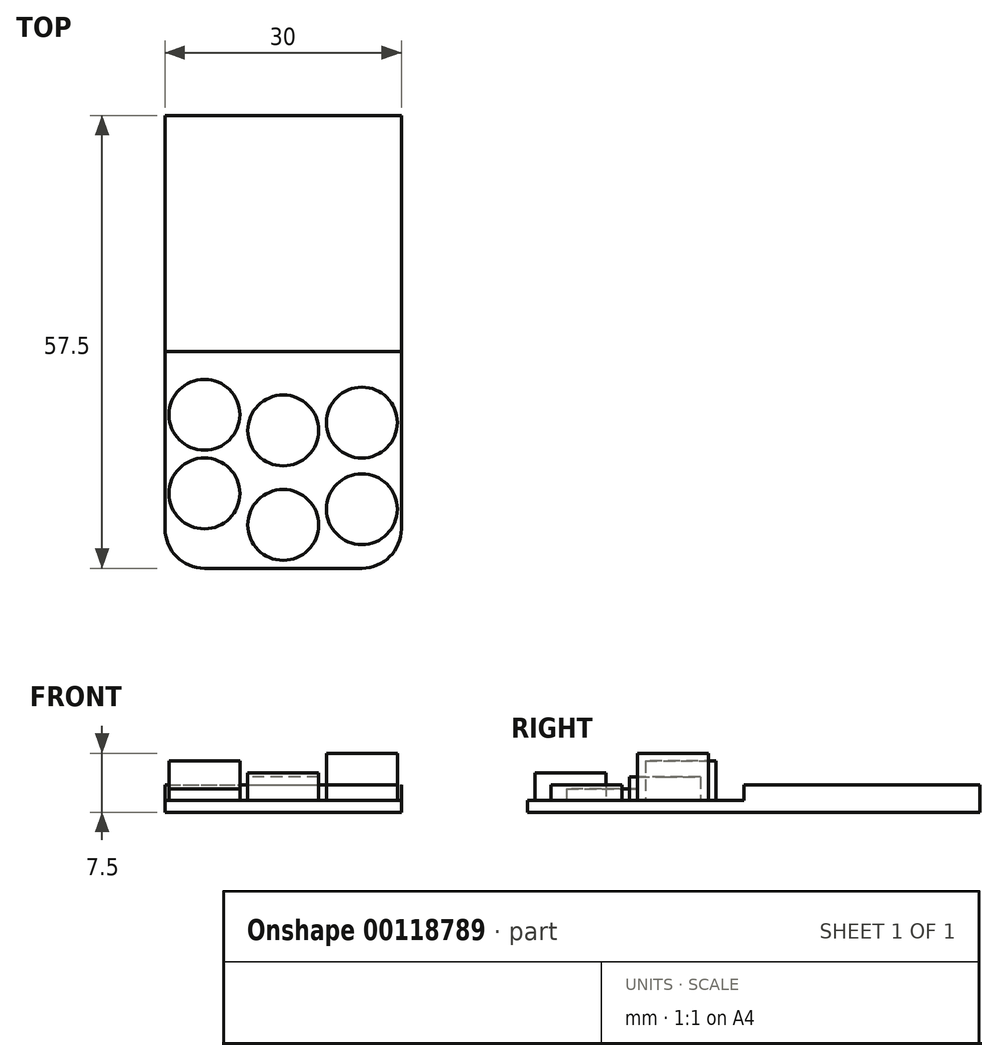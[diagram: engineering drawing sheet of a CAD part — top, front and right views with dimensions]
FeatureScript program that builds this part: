
annotation { "Feature Type Name" : "Feature", "Feature Type Description" : "" }
export const myFeature = defineFeature(function(context is Context, id is Id, definition is map)
    precondition{}
    {
        {
            var Q0;
            Q0=qCreatedBy(makeId("Top.planeOp"),FACE);
            var sketch = newSketch(context, id + "F0", { "sketchPlane" : qUnion([Q0])});
            skLineSegment(sketch, "E0.bottom", {"start": v(-15, 18.18) * mm, "end": v(15, 18.18) * mm});
            skLineSegment(sketch, "E0.top", {"start": v(-15, -11.82) * mm, "end": v(15, -11.82) * mm});
            skLineSegment(sketch, "E0.left", {"start": v(-15, 18.18) * mm, "end": v(-15, -11.82) * mm});
            skLineSegment(sketch, "E0.right", {"start": v(15, 18.18) * mm, "end": v(15, -11.82) * mm});
            skLineSegment(sketch, "E1", {"start": v(0, 18.18) * mm, "end": v(0, -11.82) * mm, "construction": true});
            skLineSegment(sketch, "E2", {"start": v(0, -11.82) * mm, "end": v(0, -39.32) * mm, "construction": true});
            skLineSegment(sketch, "E3", {"start": v(-10, -21.82) * mm, "end": v(10, -21.82) * mm, "construction": true});
            skLineSegment(sketch, "E4", {"start": v(-5, -11.82) * mm, "end": v(-5, -39.32) * mm, "construction": true});
            skLineSegment(sketch, "E5.MirrorCS", {"start": v(5, -11.82) * mm, "end": v(5, -39.32) * mm, "construction": true});
            skLineSegment(sketch, "E6", {"start": v(-10, -11.82) * mm, "end": v(-10, -39.32) * mm, "construction": true});
            skLineSegment(sketch, "E7.MirrorCS", {"start": v(10, -11.82) * mm, "end": v(10, -39.32) * mm, "construction": true});
            skPoint(sketch, "E8.orphan", {"position": v(0, -21.82) * mm});
            skCircle(sketch, "E9", {"center": v(-10, -19.82) * mm, "radius": 4.5 * mm});
            skCircle(sketch, "E10", {"center": v(0, -21.82) * mm, "radius": 4.5 * mm});
            skCircle(sketch, "E11", {"center": v(10, -20.82) * mm, "radius": 4.5 * mm});
            skLineSegment(sketch, "E12", {"start": v(-15, -11.82) * mm, "end": v(-15, -34.32) * mm});
            skLineSegment(sketch, "E13", {"start": v(-10, -39.32) * mm, "end": v(10, -39.32) * mm});
            skLineSegment(sketch, "E14", {"start": v(15, -34.32) * mm, "end": v(15, -11.82) * mm});
            skPoint(sketch, "E15.orphan", {"position": v(-10, -22.85) * mm});
            skPoint(sketch, "E16.orphan", {"position": v(-5, -28.5) * mm});
            skPoint(sketch, "E17.orphan", {"position": v(10, -22.85) * mm});
            skPoint(sketch, "E18.orphan", {"position": v(0, -31.82) * mm});
            skPoint(sketch, "E19.orphan", {"position": v(5, -28.5) * mm});
            skCircle(sketch, "E20", {"center": v(-10, -29.82) * mm, "radius": 4.5 * mm});
            skCircle(sketch, "E21", {"center": v(0, -33.82) * mm, "radius": 4.5 * mm});
            skCircle(sketch, "E22", {"center": v(10, -31.82) * mm, "radius": 4.5 * mm});
            skPoint(sketch, "E23.visualSharp", {"position": v(-15, -39.32) * mm});
            skArc(sketch, "E23.filletArc", {"start": v(-15, -34.32) * mm, "mid": v(-13.54, -37.85) * mm, "end": v(-10, -39.32) * mm});
            skPoint(sketch, "E24.visualSharp", {"position": v(15, -39.32) * mm});
            skArc(sketch, "E24.filletArc", {"start": v(10, -39.32) * mm, "mid": v(13.54, -37.85) * mm, "end": v(15, -34.32) * mm});
            skSolve(sketch);
        }
        {
            var Q0;
            Q0=makeQuery(id+"F0.imprint","IMPRINT",FACE,{"disambiguationData":[TD([[makeQuery(id+"F0.imprint","IMPRINT",EDGE,{"derivedFrom":sQuery(id+"F0.wireOp",EDGE,"E0.bottom")}),-1.0]])]});
            var Q1;
            Q1=makeQuery(id+"F0.imprint","IMPRINT",FACE,{"disambiguationData":[TD([[makeQuery(id+"F0.imprint","IMPRINT",EDGE,{"derivedFrom":sQuery(id+"F0.wireOp",EDGE,"E0.top")}),-1.0]])]});
            var Q2;
            Q2=makeQuery(id+"F0.imprint","IMPRINT",FACE,{"disambiguationData":[TD([[makeQuery(id+"F0.imprint","IMPRINT",EDGE,{"derivedFrom":sQuery(id+"F0.wireOp",EDGE,"E9")}),1.0]])]});
            var Q3;
            Q3=makeQuery(id+"F0.imprint","IMPRINT",FACE,{"disambiguationData":[TD([[makeQuery(id+"F0.imprint","IMPRINT",EDGE,{"derivedFrom":sQuery(id+"F0.wireOp",EDGE,"E10")}),1.0]])]});
            var Q4;
            Q4=makeQuery(id+"F0.imprint","IMPRINT",FACE,{"disambiguationData":[TD([[makeQuery(id+"F0.imprint","IMPRINT",EDGE,{"derivedFrom":sQuery(id+"F0.wireOp",EDGE,"E11")}),1.0]])]});
            var Q5;
            Q5=makeQuery(id+"F0.imprint","IMPRINT",FACE,{"disambiguationData":[TD([[makeQuery(id+"F0.imprint","IMPRINT",EDGE,{"derivedFrom":sQuery(id+"F0.wireOp",EDGE,"E22")}),1.0]])]});
            var Q6;
            Q6=makeQuery(id+"F0.imprint","IMPRINT",FACE,{"disambiguationData":[TD([[makeQuery(id+"F0.imprint","IMPRINT",EDGE,{"derivedFrom":sQuery(id+"F0.wireOp",EDGE,"E21")}),1.0]])]});
            var Q7;
            Q7=makeQuery(id+"F0.imprint","IMPRINT",FACE,{"disambiguationData":[TD([[makeQuery(id+"F0.imprint","IMPRINT",EDGE,{"derivedFrom":sQuery(id+"F0.wireOp",EDGE,"E20")}),1.0]])]});
            extrude(context, id + "F1", {"entities" : qUnion([Q0, Q1, Q2, Q3, Q4, Q5, Q6, Q7]), "oppositeDirection" : true, "depth" : 1.5 * mm});
        }
        {
            var Q0;
            Q0=makeQuery(id+"F0.imprint","IMPRINT",FACE,{"disambiguationData":[TD([[makeQuery(id+"F0.imprint","IMPRINT",EDGE,{"derivedFrom":sQuery(id+"F0.wireOp",EDGE,"E0.bottom")}),-1.0]])]});
            extrude(context, id + "F2", {"entities" : qUnion([Q0]), "operationType" : NewBodyOperationType.ADD, "depth" : 2 * mm});
        }
        {
            var Q0;
            Q0=makeQuery(id+"F0.imprint","IMPRINT",FACE,{"disambiguationData":[TD([[makeQuery(id+"F0.imprint","IMPRINT",EDGE,{"derivedFrom":sQuery(id+"F0.wireOp",EDGE,"E9")}),1.0]])]});
            extrude(context, id + "F3", {"entities" : qUnion([Q0]), "operationType" : NewBodyOperationType.ADD, "depth" : 5 * mm});
        }
        {
            var Q0;
            Q0=makeQuery(id+"F0.imprint","IMPRINT",FACE,{"disambiguationData":[TD([[makeQuery(id+"F0.imprint","IMPRINT",EDGE,{"derivedFrom":sQuery(id+"F0.wireOp",EDGE,"E10")}),1.0]])]});
            extrude(context, id + "F4", {"entities" : qUnion([Q0]), "operationType" : NewBodyOperationType.ADD, "depth" : 3 * mm});
        }
        {
            var Q0;
            Q0=makeQuery(id+"F0.imprint","IMPRINT",FACE,{"disambiguationData":[TD([[makeQuery(id+"F0.imprint","IMPRINT",EDGE,{"derivedFrom":sQuery(id+"F0.wireOp",EDGE,"E11")}),1.0]])]});
            extrude(context, id + "F5", {"entities" : qUnion([Q0]), "operationType" : NewBodyOperationType.ADD, "depth" : 6 * mm});
        }
        {
            var Q0;
            Q0=makeQuery(id+"F0.imprint","IMPRINT",FACE,{"disambiguationData":[TD([[makeQuery(id+"F0.imprint","IMPRINT",EDGE,{"derivedFrom":sQuery(id+"F0.wireOp",EDGE,"E22")}),1.0]])]});
            extrude(context, id + "F6", {"entities" : qUnion([Q0]), "operationType" : NewBodyOperationType.ADD, "depth" : 2 * mm});
        }
        {
            var Q0;
            Q0=makeQuery(id+"F0.imprint","IMPRINT",FACE,{"disambiguationData":[TD([[makeQuery(id+"F0.imprint","IMPRINT",EDGE,{"derivedFrom":sQuery(id+"F0.wireOp",EDGE,"E21")}),1.0]])]});
            extrude(context, id + "F7", {"entities" : qUnion([Q0]), "operationType" : NewBodyOperationType.ADD, "depth" : 3.5 * mm});
        }
        {
            var Q0;
            Q0=makeQuery(id+"F0.imprint","IMPRINT",FACE,{"disambiguationData":[TD([[makeQuery(id+"F0.imprint","IMPRINT",EDGE,{"derivedFrom":sQuery(id+"F0.wireOp",EDGE,"E20")}),1.0]])]});
            extrude(context, id + "F8", {"entities" : qUnion([Q0]), "operationType" : NewBodyOperationType.ADD, "depth" : 1.5 * mm});
        }
    });
